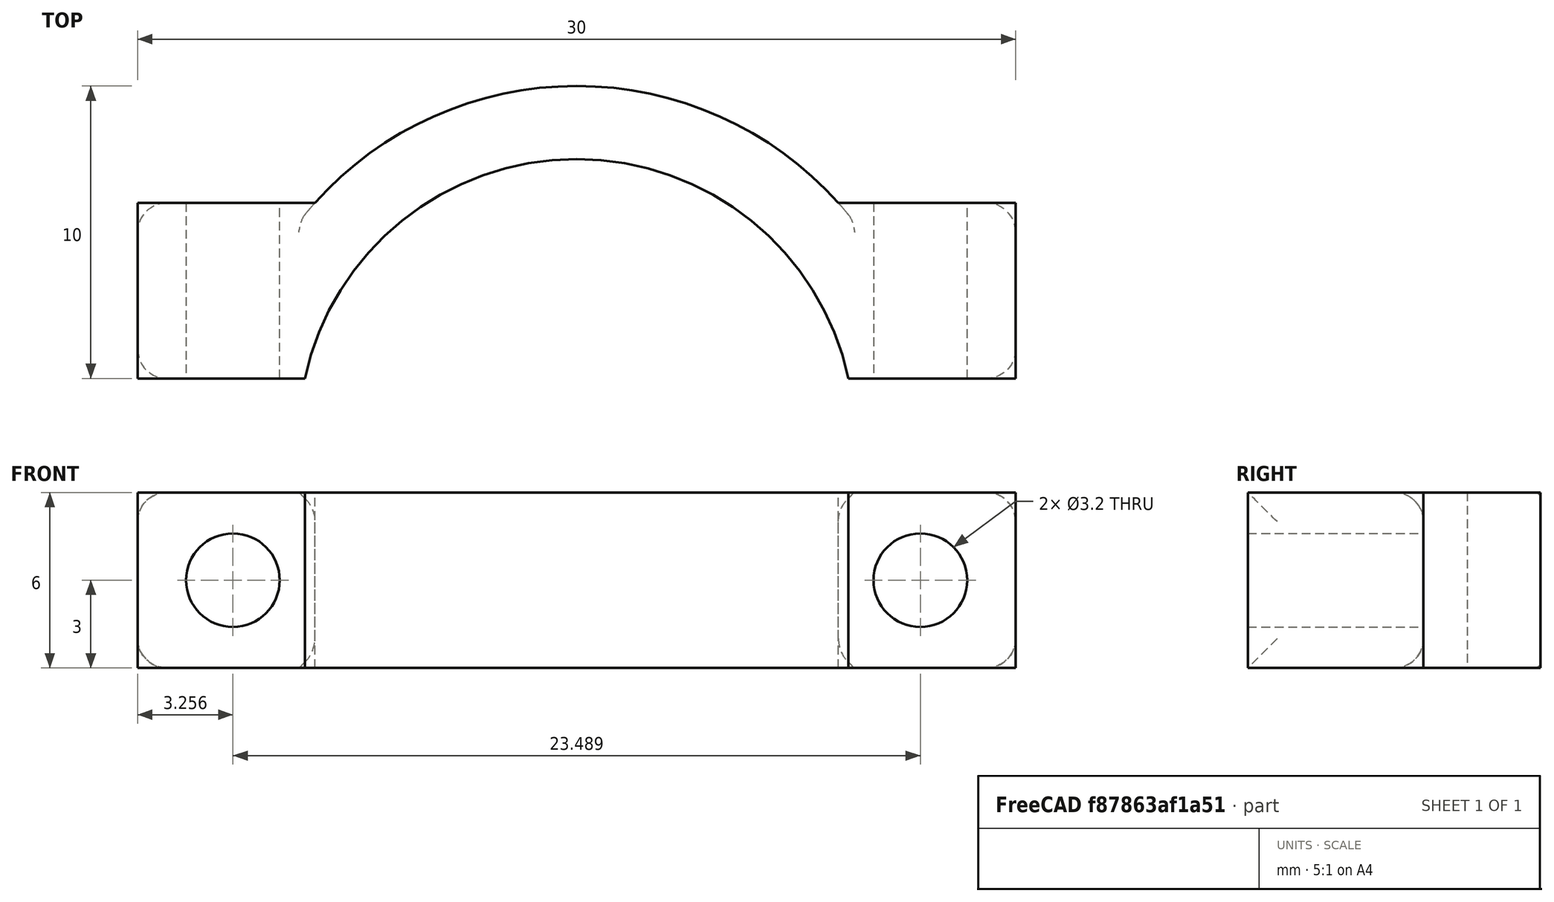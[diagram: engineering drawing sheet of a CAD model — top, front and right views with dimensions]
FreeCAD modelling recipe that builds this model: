
FCSTD DOCUMENT  (FreeCAD 0.16R)
Label: Caps30mm
License: All rights reserved
LicenseURL: http://en.wikipedia.org/wiki/All_rights_reserved
objects: PartDesign::Fillet×4, Sketcher::SketchObject×2, PartDesign::Pad×1, PartDesign::Pocket×1, Mesh::Feature×1
note: 10 computed .brp shape members not serialized (recipe doc carries the construction recipe); baked Part::Feature solids carry a one-line shape summary decoded from their .brp

FEATURE [Sketcher::SketchObject] Sketch
  sketch-geometry (8):
    g0: ArcOfCircle CenterX=0 CenterY=0 CenterZ=0 NormalX=0 NormalY=0 NormalZ=1 Radius=9.5 StartAngle=0.212113 EndAngle=2.92948
    g1: ArcOfCircle CenterX=0 CenterY=0 CenterZ=0 NormalX=0 NormalY=0 NormalZ=1 Radius=12 StartAngle=0.729728 EndAngle=2.41186
    g2: LineSegment StartX=-15 StartY=8 StartZ=0 EndX=-8.94427 EndY=8 EndZ=0
    g3: LineSegment StartX=15 StartY=8 StartZ=0 EndX=15 EndY=2 EndZ=0
    g4: LineSegment StartX=15 StartY=2 StartZ=0 EndX=9.28709 EndY=2 EndZ=0
    g5: LineSegment StartX=-15 StartY=2 StartZ=0 EndX=-15 EndY=8 EndZ=0
    g6: LineSegment StartX=8.94427 StartY=8 StartZ=0 EndX=15 EndY=8 EndZ=0
    g7: LineSegment StartX=-9.28709 StartY=2 StartZ=0 EndX=-15 EndY=2 EndZ=0
  constraints (22):
    c: Radius(g1) = 12
    c: Radius(g0) = 9.5
    c: Coincident(g0,g-1)
    c: Coincident(g1,g-1)
    c: Coincident(g6,g3)
    c: Coincident(g3,g4)
    c: Coincident(g7,g5)
    c: Coincident(g5,g2)
    c: Horizontal(g2)
    c: Horizontal(g4)
    c: Vertical(g3)
    c: Vertical(g5)
    c: DistanceX(g2,g6) = 30
    c: DistanceY(g3,g3) = 6
    c: Symmetric(g6,g2,g-2)
    c: DistanceY(g7,g-1) = -2
    c: Tangent(g2,g6)
    c: Coincident(g4,g0)
    c: Coincident(g7,g0)
    c: Tangent(g4,g7)
    c: Coincident(g2,g1)
    c: Coincident(g6,g1)
FEATURE [PartDesign::Pad] Pad
  Length = 6
  Length2 = 100
  Sketch = -> Sketch
  Type = 0
FEATURE [Sketcher::SketchObject] Sketch001
  ExternalGeometry = -> [Pad]
  Placement = pos=(0,8,0) rot=(0,0.707107,0.707107;3.14159rad)
  Support = -> Pad [Face7]
  sketch-geometry (2):
    g0: Circle CenterX=-11.7443 CenterY=3 CenterZ=0 NormalX=0 NormalY=0 NormalZ=1 Radius=1.6
    g1: Circle CenterX=11.7443 CenterY=3 CenterZ=0 NormalX=0 NormalY=0 NormalZ=1 Radius=1.6
  constraints (6):
    c: DistanceY(g-1,g0) = 3
    c: Radius(g0) = 1.6
    c: DistanceX(g0,g-5) = 2.8
    c: Radius(g1) = 1.6
    c: Distance(g1,g-7) = 3
    c: Distance(g1,g-6) = 2.8
FEATURE [PartDesign::Pocket] Pocket
  Length = 5
  Sketch = -> Sketch001
  Type = 1
FEATURE [PartDesign::Fillet] Fillet
  Base = -> Pocket [Edge4,Edge24]
  Radius = 1
FEATURE [PartDesign::Fillet] Fillet001
  Base = -> Fillet [Edge13,Edge34,Edge24,Edge8,Edge28,Edge19]
  Radius = 1
FEATURE [PartDesign::Fillet] Fillet002
  Base = -> Fillet001 [Edge17]
  Radius = 0.25
FEATURE [PartDesign::Fillet] Fillet003
  Base = -> Fillet002 [Edge14]
  Radius = 0.25
FEATURE [Mesh::Feature] Mesh  label="Fillet003 (Meshed)"
